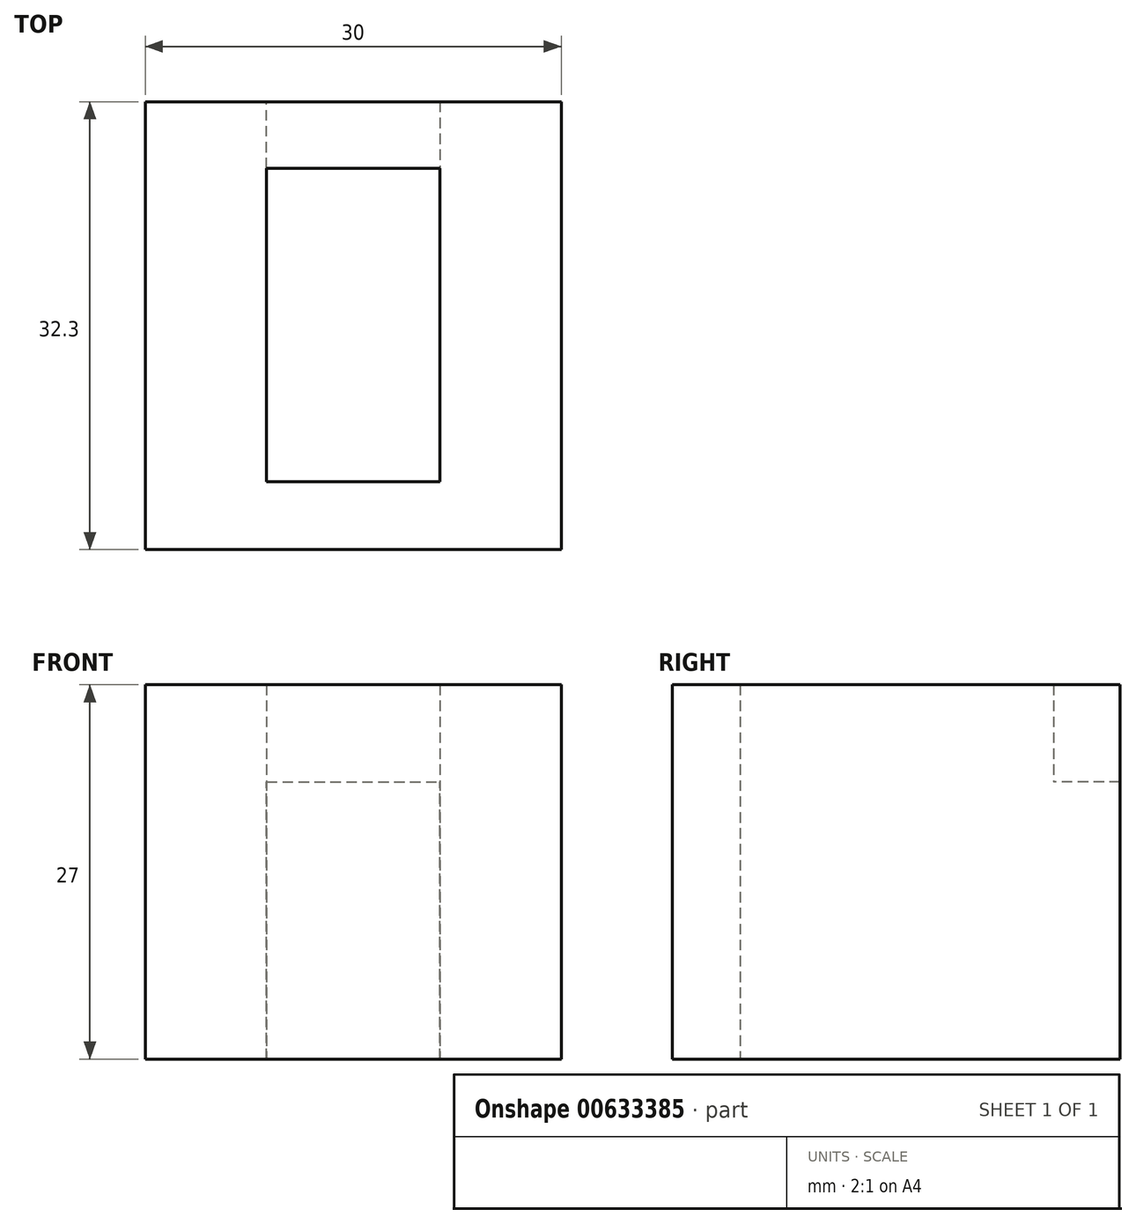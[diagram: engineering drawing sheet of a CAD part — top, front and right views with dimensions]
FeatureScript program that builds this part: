
annotation { "Feature Type Name" : "Feature", "Feature Type Description" : "" }
export const myFeature = defineFeature(function(context is Context, id is Id, definition is map)
    precondition{}
    {
        {
            var Q0;
            Q0=qCreatedBy(makeId("Top.planeOp"),FACE);
            var sketch = newSketch(context, id + "F0", { "sketchPlane" : qUnion([Q0])});
            skLineSegment(sketch, "E0.bottom", {"start": v(0, 0) * mm, "end": v(12.5, 0) * mm});
            skLineSegment(sketch, "E0.top", {"start": v(0, 22.6) * mm, "end": v(12.5, 22.6) * mm});
            skLineSegment(sketch, "E0.left", {"start": v(0, 0) * mm, "end": v(0, 22.6) * mm});
            skLineSegment(sketch, "E0.right", {"start": v(12.5, 0) * mm, "end": v(12.5, 22.6) * mm});
            skSolve(sketch);
        }
        {
            var Q0;
            Q0=qCreatedBy(makeId("Top.planeOp"),FACE);
            var sketch = newSketch(context, id + "F1", { "sketchPlane" : qUnion([Q0])});
            skLineSegment(sketch, "E1", {"start": v(-8.75, -4.9) * mm, "end": v(-8.75, 27.4) * mm});
            skLineSegment(sketch, "E2", {"start": v(-8.75, 27.4) * mm, "end": v(21.25, 27.4) * mm});
            skLineSegment(sketch, "E3", {"start": v(21.25, 27.4) * mm, "end": v(21.25, -4.9) * mm});
            skLineSegment(sketch, "E4", {"start": v(21.25, -4.9) * mm, "end": v(-8.75, -4.9) * mm});
            skSolve(sketch);
        }
        {
            var Q0;
            Q0 = qSketchRegion(id + "F1", true);
            extrude(context, id + "F2", {"entities" : qUnion([Q0]), "depth" : 7 * mm, "offsetDistance" : 25 * mm});
        }
        {
            var Q0;
            Q0 = qSketchRegion(id + "F0", true);
            extrude(context, id + "F3", {"entities" : qUnion([Q0]), "operationType" : NewBodyOperationType.REMOVE, "depth" : 7 * mm, "offsetDistance" : 25 * mm});
        }
        {
            var Q0;
            Q0=qCreatedBy(makeId("Top.planeOp"),FACE);
            var sketch = newSketch(context, id + "F4", { "sketchPlane" : qUnion([Q0])});
            skPoint(sketch, "E5", {"position": v(12.5, 0) * mm});
            skPoint(sketch, "E6", {"position": v(0, 22.6) * mm});
            skPoint(sketch, "E7", {"position": v(12.5, 22.6) * mm});
            skPoint(sketch, "E8", {"position": v(-8.75, -4.9) * mm});
            skPoint(sketch, "E9", {"position": v(21.25, -4.9) * mm});
            skPoint(sketch, "E10", {"position": v(21.25, 27.4) * mm});
            skPoint(sketch, "E11", {"position": v(-8.75, 27.4) * mm});
            skLineSegment(sketch, "E12.bottom", {"start": v(0, 0) * mm, "end": v(-8.75, 0) * mm});
            skLineSegment(sketch, "E12.top", {"start": v(0, -4.9) * mm, "end": v(-8.75, -4.9) * mm});
            skLineSegment(sketch, "E12.left", {"start": v(0, 0) * mm, "end": v(0, -4.9) * mm});
            skLineSegment(sketch, "E12.right", {"start": v(-8.75, 0) * mm, "end": v(-8.75, -4.9) * mm});
            skLineSegment(sketch, "E13.bottom", {"start": v(12.5, 0) * mm, "end": v(21.25, 0) * mm});
            skLineSegment(sketch, "E13.top", {"start": v(12.5, -4.9) * mm, "end": v(21.25, -4.9) * mm});
            skLineSegment(sketch, "E13.left", {"start": v(12.5, 0) * mm, "end": v(12.5, -4.9) * mm});
            skLineSegment(sketch, "E13.right", {"start": v(21.25, 0) * mm, "end": v(21.25, -4.9) * mm});
            skLineSegment(sketch, "E14.bottom", {"start": v(21.25, 27.4) * mm, "end": v(12.5, 27.4) * mm});
            skLineSegment(sketch, "E14.top", {"start": v(21.25, 22.6) * mm, "end": v(12.5, 22.6) * mm});
            skLineSegment(sketch, "E14.left", {"start": v(21.25, 27.4) * mm, "end": v(21.25, 22.6) * mm});
            skLineSegment(sketch, "E14.right", {"start": v(12.5, 27.4) * mm, "end": v(12.5, 22.6) * mm});
            skLineSegment(sketch, "E15.bottom", {"start": v(0, 22.6) * mm, "end": v(-8.75, 22.6) * mm});
            skLineSegment(sketch, "E15.top", {"start": v(0, 27.4) * mm, "end": v(-8.75, 27.4) * mm});
            skLineSegment(sketch, "E15.left", {"start": v(0, 22.6) * mm, "end": v(0, 27.4) * mm});
            skLineSegment(sketch, "E15.right", {"start": v(-8.75, 22.6) * mm, "end": v(-8.75, 27.4) * mm});
            skLineSegment(sketch, "E16.left", {"start": v(0, 0) * mm, "end": v(0, 22.6) * mm});
            skLineSegment(sketch, "E16.right", {"start": v(-8.75, 0) * mm, "end": v(-8.75, 22.6) * mm});
            skLineSegment(sketch, "E17.bottom", {"start": v(0, 0) * mm, "end": v(12.5, 0) * mm});
            skLineSegment(sketch, "E17.top", {"start": v(0, -4.9) * mm, "end": v(12.5, -4.9) * mm});
            skLineSegment(sketch, "E18.bottom", {"start": v(21.25, 0) * mm, "end": v(12.5, 0) * mm});
            skLineSegment(sketch, "E18.left", {"start": v(21.25, 0) * mm, "end": v(21.25, 22.6) * mm});
            skLineSegment(sketch, "E18.right", {"start": v(12.5, 0) * mm, "end": v(12.5, 22.6) * mm});
            skSolve(sketch);
        }
        {
            var Q0;
            Q0 = qSketchRegion(id + "F4", true);
            extrude(context, id + "F5", {"entities" : qUnion([Q0]), "operationType" : NewBodyOperationType.ADD, "oppositeDirection" : true, "depth" : 20 * mm, "offsetDistance" : 25 * mm});
        }
    });
